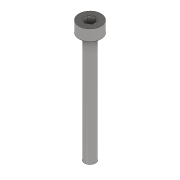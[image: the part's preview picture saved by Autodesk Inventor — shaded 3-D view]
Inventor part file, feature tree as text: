
AUTODESK INVENTOR PART (.ipt)
format: ipt  version: 2022 (Build 260153000, 153)  size: 95,232 bytes
history: native  units: mm
features: extrude x3, sketch x3
ambient origin geometry x8: Origin, YZ Plane, XZ Plane, XY Plane, X Axis, Y Axis, Z Axis, Center Point
bodies: Solid1 (feature_tree)
feature tree (6):
  extrude  "Extrusion1"  Depth=20.0mm TaperAngle=0.0deg
  extrude  "Extrusion2"  Depth=2.0mm TaperAngle=0.0deg
  extrude  "Extrusion3"  [1 undecoded]
  sketch  "Sketch1"  dims[d0=2.0mm d1=20.0mm d2=0.0mm]
  sketch  "Sketch2"  dims[d3=4.0mm d4=2.0mm d5=0.0mm]
  sketch  "Sketch3"  dims[d6=1.0mm d7=0.0mm]
note: 1 required parameter value undecoded (feature->parameter linkage not recoverable at this tier; creation-order binding heuristic only, values carry confidence <= 0.55)
